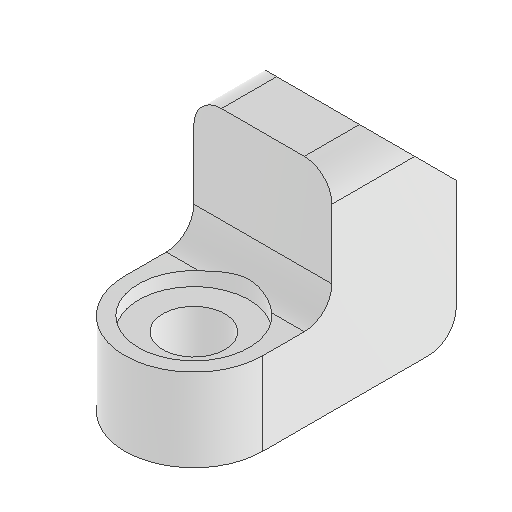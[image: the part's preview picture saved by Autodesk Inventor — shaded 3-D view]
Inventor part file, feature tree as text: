
AUTODESK INVENTOR PART (.ipt)
format: ipt  version: 2025.2 (Build 292293000, 293)  size: 139,264 bytes
history: native  units: in
note: dims shown in document units (in); Inventor stores cm internally (conversion verified against a paired STEP export)
features: sketch x2, extrude x2, hole x1, chamfer x1, fillet x1
ambient origin geometry x8: Origin, YZ Plane, XZ Plane, XY Plane, X Axis, Y Axis, Z Axis, Center Point
bodies: Solid1 (feature_tree)
feature tree (7):
  sketch  "Sketch1"  dims[d0=0.3937in d1=0.748in]
  extrude  "Extrusion1"  Depth=0.3937in
  extrude  "Extrusion2"  Depth=0.0787in
  hole  "Hole1"  [1 undecoded]
  chamfer  "Chamfer1"  Distance=0.3543in
  fillet  "Fillet1"  [1 undecoded]
  sketch  "Sketch2"  dims[d2=0.3543in d3=0.1772in d4=0.5906in d5=0.0in d6=0.3543in d7=0.0in d8=0.1772in d9=0.315in d10=0.315in d11=0.0394in d12=90.0deg d13=0.315in d14=0.8108in d15=0.1969in d16=0.0787in d17=45.0deg d24=0.2756in d25=0.0787in d21=0.0in d22=0.0in d23=0.0in d26=0.0in d27=0.0in]
note: 2 required parameter values undecoded (feature->parameter linkage not recoverable at this tier; creation-order binding heuristic only, values carry confidence <= 0.55)
